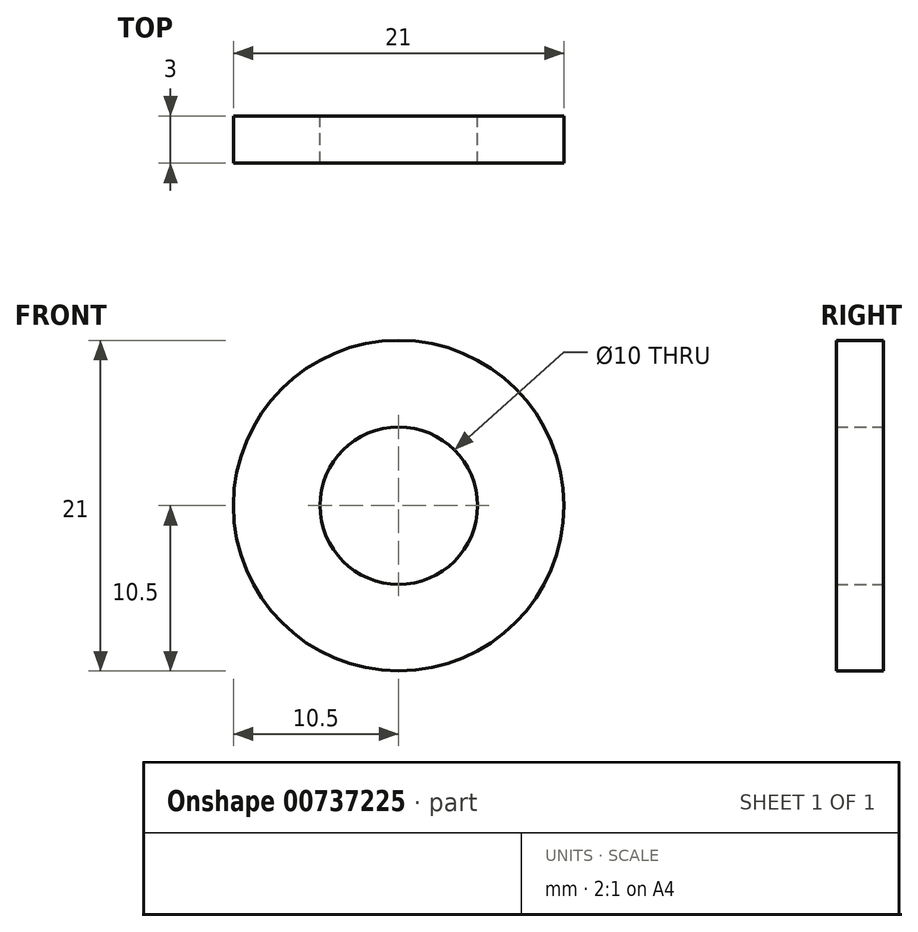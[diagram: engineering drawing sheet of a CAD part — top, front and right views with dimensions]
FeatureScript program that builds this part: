
annotation { "Feature Type Name" : "Feature", "Feature Type Description" : "" }
export const myFeature = defineFeature(function(context is Context, id is Id, definition is map)
    precondition{}
    {
        {
            var Q0;
            Q0=qCreatedBy(makeId("Front.planeOp"),FACE);
            var sketch = newSketch(context, id + "F0", { "sketchPlane" : qUnion([Q0])});
            skCircle(sketch, "E0", {"center": v(0, 0) * mm, "radius": 10.5 * mm});
            skCircle(sketch, "E1", {"center": v(0, 0) * mm, "radius": 5 * mm});
            skSolve(sketch);
        }
        {
            var Q0;
            Q0=makeQuery(id+"F0.imprint","IMPRINT",FACE,{"disambiguationData":[TD([[makeQuery(id+"F0.imprint","IMPRINT",EDGE,{"derivedFrom":sQuery(id+"F0.wireOp",EDGE,"E0")}),1.0]])]});
            extrude(context, id + "F1", {"entities" : qUnion([Q0]), "endBound" : BoundingType.SYMMETRIC, "depth" : 3 * mm, "offsetDistance" : 25 * mm});
        }
    });
